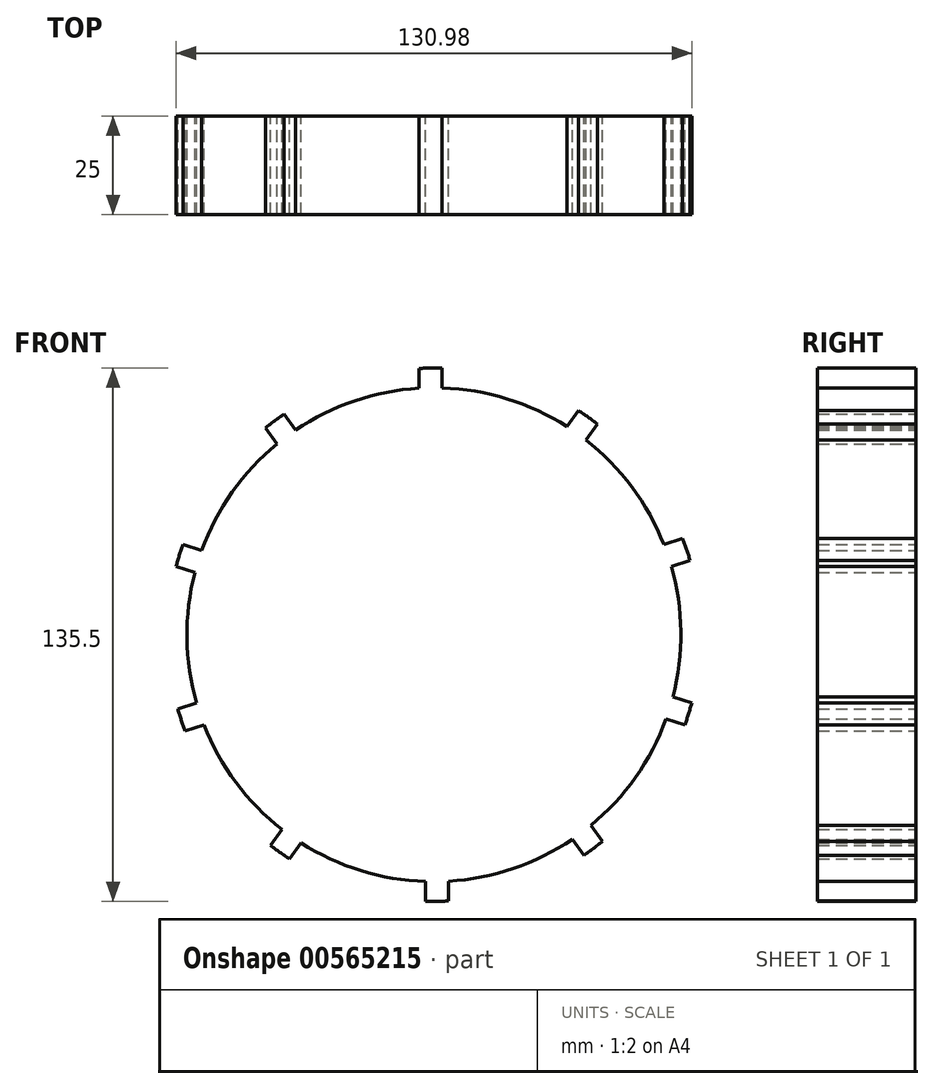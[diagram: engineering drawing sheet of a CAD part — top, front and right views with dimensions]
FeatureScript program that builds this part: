
annotation { "Feature Type Name" : "Feature", "Feature Type Description" : "" }
export const myFeature = defineFeature(function(context is Context, id is Id, definition is map)
    precondition{}
    {
        {
            var Q0;
            Q0=qCreatedBy(makeId("Front.planeOp"),FACE);
            var sketch = newSketch(context, id + "F0", { "sketchPlane" : qUnion([Q0])});
            skArc(sketch, "E0", {"start": v(60.73, -15.8) * mm, "mid": v(62.74, 0.82) * mm, "end": v(60.3, 17.37) * mm});
            skArc(sketch, "E1.0", {"start": v(2.11, 67.72) * mm, "mid": v(-0.82, 67.75) * mm, "end": v(-3.74, 67.65) * mm});
            skLineSegment(sketch, "E2", {"start": v(-3.74, 67.65) * mm, "end": v(-3.74, 62.64) * mm});
            skLineSegment(sketch, "E3", {"start": v(2.11, 67.72) * mm, "end": v(2.11, 62.71) * mm});
            skLineSegment(sketch, "E4", {"start": v(2.11, 62.71) * mm, "end": v(2.11, 65.22) * mm});
            skLineSegment(sketch, "E5.1.0", {"start": v(-38.1, 56.03) * mm, "end": v(-35.15, 51.98) * mm});
            skLineSegment(sketch, "E5.1.1", {"start": v(-42.8, 52.53) * mm, "end": v(-39.85, 48.47) * mm});
            skLineSegment(sketch, "E5.2.0", {"start": v(-63.75, 22.93) * mm, "end": v(-59, 21.39) * mm});
            skLineSegment(sketch, "E5.2.1", {"start": v(-65.5, 17.34) * mm, "end": v(-60.73, 15.8) * mm});
            skLineSegment(sketch, "E5.3.0", {"start": v(-65.06, -18.92) * mm, "end": v(-60.3, -17.37) * mm});
            skLineSegment(sketch, "E5.3.1", {"start": v(-63.18, -24.46) * mm, "end": v(-58.42, -22.92) * mm});
            skLineSegment(sketch, "E5.4.0", {"start": v(-41.51, -53.54) * mm, "end": v(-38.57, -49.5) * mm});
            skLineSegment(sketch, "E5.4.1", {"start": v(-36.73, -56.93) * mm, "end": v(-33.79, -52.88) * mm});
            skLineSegment(sketch, "E5.5.0", {"start": v(-2.11, -67.72) * mm, "end": v(-2.11, -62.71) * mm});
            skLineSegment(sketch, "E5.5.1", {"start": v(3.74, -67.65) * mm, "end": v(3.74, -62.64) * mm});
            skLineSegment(sketch, "E5.6.0", {"start": v(38.1, -56.03) * mm, "end": v(35.15, -51.98) * mm});
            skLineSegment(sketch, "E5.6.1", {"start": v(42.8, -52.53) * mm, "end": v(39.85, -48.47) * mm});
            skLineSegment(sketch, "E5.7.0", {"start": v(63.75, -22.93) * mm, "end": v(59, -21.39) * mm});
            skLineSegment(sketch, "E5.7.1", {"start": v(65.5, -17.34) * mm, "end": v(60.73, -15.8) * mm});
            skLineSegment(sketch, "E5.8.0", {"start": v(65.06, 18.92) * mm, "end": v(60.3, 17.37) * mm});
            skLineSegment(sketch, "E5.8.1", {"start": v(63.18, 24.46) * mm, "end": v(58.42, 22.92) * mm});
            skLineSegment(sketch, "E5.9.0", {"start": v(41.51, 53.54) * mm, "end": v(38.57, 49.5) * mm});
            skLineSegment(sketch, "E5.9.1", {"start": v(36.73, 56.93) * mm, "end": v(33.79, 52.88) * mm});
            skArc(sketch, "E6.trimOffspring", {"start": v(41.51, 53.54) * mm, "mid": v(39.16, 55.29) * mm, "end": v(36.73, 56.93) * mm});
            skArc(sketch, "E7.trimOffspring", {"start": v(65.06, 18.92) * mm, "mid": v(64.18, 21.71) * mm, "end": v(63.18, 24.46) * mm});
            skArc(sketch, "E8.trimOffspring", {"start": v(-38.1, 56.03) * mm, "mid": v(-40.48, 54.33) * mm, "end": v(-42.8, 52.53) * mm});
            skArc(sketch, "E9.trimOffspring", {"start": v(-63.75, 22.93) * mm, "mid": v(-64.68, 20.16) * mm, "end": v(-65.5, 17.34) * mm});
            skArc(sketch, "E10.trimOffspring", {"start": v(-65.06, -18.92) * mm, "mid": v(-64.18, -21.71) * mm, "end": v(-63.18, -24.46) * mm});
            skArc(sketch, "E11.trimOffspring", {"start": v(-41.51, -53.54) * mm, "mid": v(-39.16, -55.29) * mm, "end": v(-36.73, -56.93) * mm});
            skArc(sketch, "E12.trimOffspring", {"start": v(-2.11, -67.72) * mm, "mid": v(0.82, -67.75) * mm, "end": v(3.74, -67.65) * mm});
            skArc(sketch, "E13.trimOffspring", {"start": v(38.1, -56.03) * mm, "mid": v(40.48, -54.33) * mm, "end": v(42.8, -52.53) * mm});
            skArc(sketch, "E14.trimOffspring", {"start": v(63.75, -22.93) * mm, "mid": v(64.68, -20.16) * mm, "end": v(65.5, -17.34) * mm});
            skArc(sketch, "E15.trimOffspring", {"start": v(39.85, -48.47) * mm, "mid": v(51.24, -36.22) * mm, "end": v(59, -21.39) * mm});
            skArc(sketch, "E16.trimOffspring", {"start": v(3.74, -62.64) * mm, "mid": v(20.17, -59.42) * mm, "end": v(35.15, -51.98) * mm});
            skArc(sketch, "E17.trimOffspring", {"start": v(-33.79, -52.88) * mm, "mid": v(-18.61, -59.93) * mm, "end": v(-2.11, -62.71) * mm});
            skArc(sketch, "E18.trimOffspring", {"start": v(-58.42, -22.92) * mm, "mid": v(-50.28, -37.54) * mm, "end": v(-38.57, -49.5) * mm});
            skArc(sketch, "E19.trimOffspring", {"start": v(-60.73, 15.8) * mm, "mid": v(-62.74, -0.82) * mm, "end": v(-60.3, -17.37) * mm});
            skArc(sketch, "E20.trimOffspring", {"start": v(58.42, 22.92) * mm, "mid": v(50.28, 37.54) * mm, "end": v(38.57, 49.5) * mm});
            skArc(sketch, "E21.trimOffspring", {"start": v(33.79, 52.88) * mm, "mid": v(18.61, 59.93) * mm, "end": v(2.11, 62.71) * mm});
            skArc(sketch, "E22.trimOffspring", {"start": v(-3.74, 62.64) * mm, "mid": v(-20.17, 59.42) * mm, "end": v(-35.15, 51.98) * mm});
            skArc(sketch, "E23.trimOffspring", {"start": v(-39.85, 48.47) * mm, "mid": v(-51.24, 36.22) * mm, "end": v(-59, 21.39) * mm});
            skSolve(sketch);
        }
        {
            var Q0;
            Q0=makeQuery(id+"F0.imprint","IMPRINT",FACE,{"disambiguationData":[TD([[makeQuery(id+"F0.imprint","IMPRINT",EDGE,{"derivedFrom":sQuery(id+"F0.wireOp",EDGE,"E0")}),1.0]])]});
            extrude(context, id + "F1", {"entities" : qUnion([Q0]), "depth" : 25 * mm, "offsetDistance" : 25 * mm});
        }
    });
